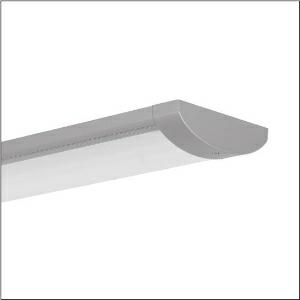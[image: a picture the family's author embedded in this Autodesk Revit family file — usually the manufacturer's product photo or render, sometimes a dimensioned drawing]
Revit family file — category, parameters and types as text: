
# Revit family: tv_20_5xa861d4n0j
name_source: partatom
category: Lighting Fixtures
units: mm (PartAtom-declared; Revit-internal decimal feet)

## family parameters
Cut with Voids When Loaded = No
Host = Face
Light Source = No
Part Type = Normal
Room Calculation Point = No
Round Connector Dimension = Use Diameter
Shared = No

## types (1)
- TV 20 (1 x LED 4000K / CRI = 80 (unbekannt), 3960 lm, 4000K)
    Apparent Load = 37 VA
    CIE Flux Codes = 48 78 95 99 100
    Color Rendering = 80
    Color Temperature = 4000K
    Default Elevation = 1800 mm
    Description = TV 20, vandal-proof luminaire, primary light control with specular reflector, of aluminium, matt, primary optical cover: enclosure, of PC, frosted, light emission: direct distribution, primary light characteristic: symmetric, installation type: surface-mounted, LED, rated luminous flux: 3.960lm, luminous efficacy: 107lm/W, light colour: 840, colour temperature: 4000K, control gear: DALI, mains connection: 230V, AC, 50Hz, rated input power: 37W, luminaire housing, of aluminium, coated, Siteco® metallic grey (DB 702S), with wall and ceiling fixing element, length: 1.261mm, width: 260mm, height: 70mm, mounting height: 2.5..4.0m, protection rating (complete): IP65, insulation class (complete): insulation class I (protective earthing), certification: CE, protection symbol: F, impact resistance: 2x IK10, standard: EN 60598, packaging unit: 1 piece
    Height = 70 mm
    Lamp = 1 x LED 4000K / CRI >= 80 (unbekannt)
    Lamp Light Flux = 3960 lm
    Lamp count = 1
    Length = 1261 mm
    Luminous efficacy = 107 lm/W
    Manufacturer = Siteco
    ModVariant = No
    Model = 5XA861D4N0J
    Mounting Place = Ceiling
    Mounting Type = Surface mounted
    Number of Poles = 1
    OnlyDefault = Yes
    Power Factor = 1
    Product Name = TV 20
    Product group = vandal-proof luminaire
    ProductGroupID = 310
    Protection Class = Protection class I
    Protection Degree = IP 65
    RLX_Detail_Level = 1
    RLX_Emergency_Light_Flux = 0 lm
    RLX_Emergency_Type = 0
    RLX_Emergency_Type_DB = No
    RlxData = <blob elided: 25617 chars, md5=55f4ec54>
    Socket = socket
    Standby Power = 0 W
    System Light Flux = 3960 lm
    System Power = 37 W
    Type Comments = Product without accessories
    Type Image = l_1004809.jpg
    URL = http://relux.com
    VarID = ---
    Voltage = 0 V
    Weight = 0.00 kg
    Width = 260 mm

## geometry (parser evidence)
native form markers: Blend x4, Sweep x11
no freeform markers — native parametric forms only
